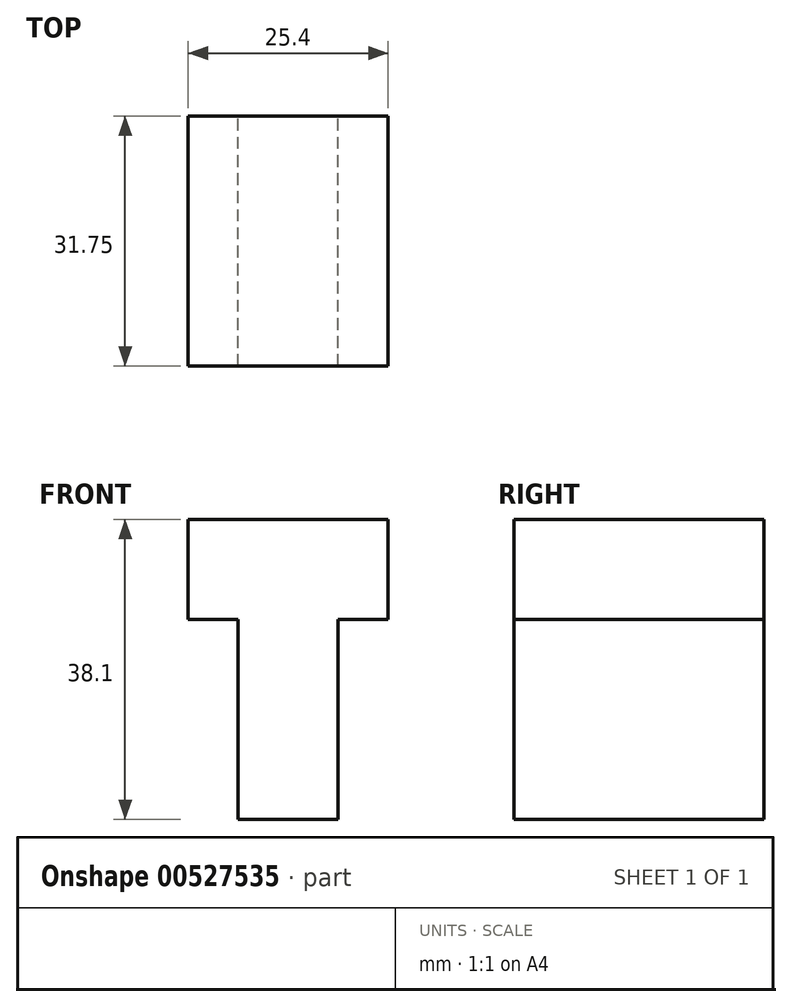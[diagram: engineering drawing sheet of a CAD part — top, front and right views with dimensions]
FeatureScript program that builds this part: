
annotation { "Feature Type Name" : "Feature", "Feature Type Description" : "" }
export const myFeature = defineFeature(function(context is Context, id is Id, definition is map)
    precondition{}
    {
        {
            var Q0;
            Q0=qCreatedBy(makeId("Front.planeOp"),FACE);
            var sketch = newSketch(context, id + "F0", { "sketchPlane" : qUnion([Q0])});
            skLineSegment(sketch, "E0", {"start": v(0, 0) * mm, "end": v(0, 25.4) * mm});
            skLineSegment(sketch, "E1", {"start": v(0, 25.4) * mm, "end": v(-6.35, 25.4) * mm});
            skLineSegment(sketch, "E2", {"start": v(-6.35, 25.4) * mm, "end": v(-6.35, 38.1) * mm});
            skLineSegment(sketch, "E3", {"start": v(-6.35, 38.1) * mm, "end": v(19.05, 38.1) * mm});
            skLineSegment(sketch, "E4", {"start": v(19.05, 38.1) * mm, "end": v(19.05, 25.4) * mm});
            skLineSegment(sketch, "E5", {"start": v(19.05, 25.4) * mm, "end": v(12.7, 25.4) * mm});
            skLineSegment(sketch, "E6", {"start": v(12.7, 25.4) * mm, "end": v(12.7, 0) * mm});
            skLineSegment(sketch, "E7", {"start": v(12.7, 0) * mm, "end": v(0, 0) * mm});
            skSolve(sketch);
        }
        {
            var Q0;
            Q0=makeQuery(id+"F0.imprint","IMPRINT",FACE,{"disambiguationData":[TD([[makeQuery(id+"F0.imprint","IMPRINT",EDGE,{"derivedFrom":sQuery(id+"F0.wireOp",EDGE,"E0")}),-1.0]])]});
            extrude(context, id + "F1", {"entities" : qUnion([Q0]), "depth" : 31.75 * mm, "offsetDistance" : 25.4 * mm});
        }
    });
